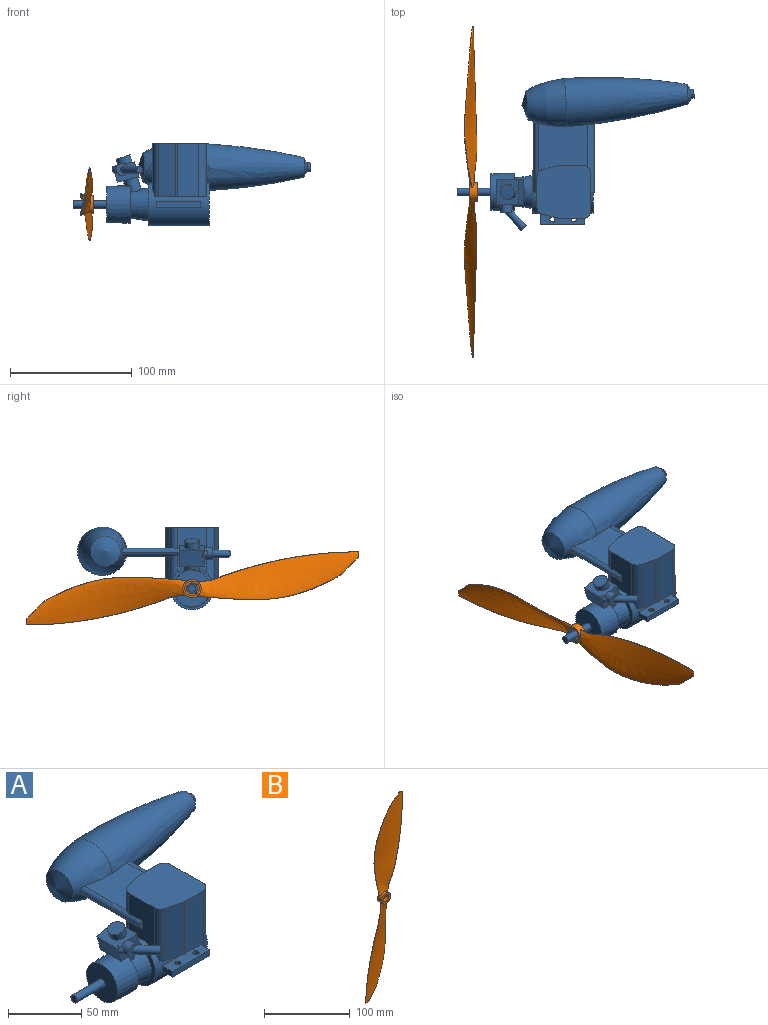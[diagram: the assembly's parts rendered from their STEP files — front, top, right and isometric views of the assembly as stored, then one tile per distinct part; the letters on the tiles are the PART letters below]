
ASSEMBLY  parts=2 mates=1
PART A: 76 faces, bbox 194.5x125.9x68.3 mm
  f0: cylinder r=17.5mm len=50mm, axis (-1,0,0), area 3318.5mm2, adj f38,f39,f40,f41,f42,f43,f47,f48
  f1: cylinder r=3mm len=18.55mm, axis (-0.68,0.74,0), area 335.6mm2, adj f2,f4,f12
  f2: plane 6x4.42mm, normal (0.68,-0.74,0), area 28.3mm2, adj f1
  f3: plane 20.3x16.69mm, normal (0,-1,0), area 153.9mm2, adj f4,f5,f6,f7,f8,f16
  f4: cylinder r=4.89mm len=9.78mm, axis (0,1,0), area 186.2mm2, adj f1,f3,f9,f11,f12,f16
  f5: plane 20.56x17.83mm, normal (-0.22,0,0.98), area 252mm2, adj f3,f6,f8,f9,f10,f11,f13,f14
  f6: plane 20.56x12.88mm, normal (-0.96,0,-0.28), area 261.1mm2, adj f3,f5,f7,f9,f10,f15,f16
  f7: plane 20.62x18.15mm, normal (0.22,0,-0.98), area 258.4mm2, adj f3,f6,f8,f10,f59
  f8: plane 20.32x12.51mm, normal (0.95,0,0.3), area 266.3mm2, adj f3,f5,f7,f10
  f9: plane 3.86x2.28mm, normal (0,-1,0), area 2.2mm2, adj f4,f5,f6,f16
  f10: plane 21.5x16.55mm, normal (0,1,0), area 237.9mm2, adj f5,f6,f7,f8
  f11: plane 5.69x1.69mm, normal (0,1,0), area 3.8mm2, adj f4,f5
  f12: plane 9.78x8.96mm, normal (0,-1,0), area 46.2mm2, adj f1,f4
  f13: plane 1.05x0.96mm, normal (-0.68,0.74,0), area 0.1mm2, adj f5,f14
  f14: cylinder r=3mm len=1.46mm, axis (-0.68,0.74,0), area 0.6mm2, adj f5,f13
  f15: plane 4.77x1.82mm, normal (-0.68,0.74,0), area 5.2mm2, adj f6,f16
  f16: cylinder r=3mm len=5.95mm, axis (-0.68,0.74,0), area 26.2mm2, adj f3,f4,f6,f9,f15
  f17: plane 6.12x2.44mm, normal (0,-1,0), area 10.4mm2, adj f29,f30,f54
  f18: cone r=3.59mm half-angle=59.2deg, axis (-1,-0.07,0), area 188.1mm2, adj f19,f23
  f19: cylinder r=3.59mm len=7.33mm, axis (-1,-0.07,0), area 55.4mm2, adj f18,f20
  f20: plane 7.18x7.16mm, normal (1,0.07,0), area 40.4mm2, adj f19
  f21: cone r=0mm half-angle=70.2deg, axis (1,0.07,0), area 501.9mm2, adj f22
  f22: revolved ~39.86x39.85mm, area 3408.9mm2, adj f21,f23,f24,f25,f29,f30
  f23: revolved ~101.71x40.61mm, area 9871mm2, adj f18,f22,f24,f25,f27,f28
  f24: plane 40.69x39.9mm, normal (0,0,-1), area 1339.5mm2, adj f22,f23,f27,f29,f32,f33,f34,f40
  f25: plane 40.76x40.24mm, normal (0,0,1), area 1330.5mm2, adj f22,f23,f28,f30,f50,f51,f52,f55
  f26: plane 5.19x2.82mm, normal (0,-1,0), area 8.8mm2, adj f27,f28,f53
  f27: cylinder r=6.67mm len=56.25mm, axis (0,-1,0), area 327.2mm2, adj f23,f24,f26,f28,f41,f53
  f28: cylinder r=6.67mm len=56.25mm, axis (0,-1,0), area 326.4mm2, adj f23,f25,f26,f27,f53,f56
  f29: cylinder r=3.68mm len=57.78mm, axis (0,-1,0), area 290.2mm2, adj f17,f22,f24,f30,f40,f54
  f30: cylinder r=3.68mm len=57.78mm, axis (0,-1,0), area 288.7mm2, adj f17,f22,f25,f29,f54,f55
  f31: plane 44x44mm, normal (0,0,1), area 1815.3mm2, adj f35,f36,f37,f42,f43,f50,f51,f52
  f32: plane 20.21x13.53mm, normal (-0.25,0.97,0), area 282.5mm2, adj f24,f33,f39,f40
  f33: cylinder r=6.35mm len=20.21mm, axis (0,0,-1), area 32.5mm2, adj f24,f32,f34,f39
  f34: plane 20.21x17.77mm, normal (0,1,0), area 359.1mm2, adj f24,f33,f39,f41
  f35: plane 43.65x17.77mm, normal (0,-1,0), area 775.5mm2, adj f31,f36,f38,f42
  f36: cylinder r=6.35mm len=43.65mm, axis (0,0,-1), area 70.1mm2, adj f31,f35,f37,f38
  f37: plane 43.65x13.53mm, normal (-0.25,-0.97,0), area 610.1mm2, adj f31,f36,f38,f43
  f38: plane 42.42x5.69mm, normal (0,0,-1), area 192.2mm2, adj f0,f35,f36,f37,f42,f43
  f39: plane 42.42x5.69mm, normal (0,0,-1), area 192.2mm2, adj f0,f32,f33,f34,f40,f41
  f40: cylinder r=6.35mm len=20.42mm, axis (0,0,-1), area 153.9mm2, adj f0,f24,f29,f32,f39,f54
  f41: cylinder r=6.35mm len=20.89mm, axis (0,0,-1), area 203.3mm2, adj f0,f24,f27,f34,f39,f53
  f42: cylinder r=6.35mm len=43.65mm, axis (0,0,-1), area 434.9mm2, adj f0,f31,f35,f38,f53
  f43: cylinder r=6.35mm len=43.65mm, axis (0,0,-1), area 349.6mm2, adj f0,f31,f37,f38,f54
  f44: plane 6x6mm, normal (-1,0,0), area 28.3mm2, adj f45
  f45: cylinder r=3mm len=27mm, axis (1,0,0), area 508.9mm2, adj f44,f49
  f46: plane 31.12x30.02mm, normal (1,0,0), area 294.5mm2, adj f57,f58,f59
  f47: plane 35x35mm, normal (-1,0,0), area 389.6mm2, adj f0,f57
  f48: plane 35x35mm, normal (1,0,0), area 962.1mm2, adj f0
  f49: plane 30x30mm, normal (-1,0,0), area 678.6mm2, adj f45,f58
  f50: plane 16.9x13.53mm, normal (-0.25,0.97,0), area 236.2mm2, adj f25,f31,f51,f55
  f51: cylinder r=6.35mm len=16.9mm, axis (0,0,-1), area 27.1mm2, adj f25,f31,f50,f52
  f52: plane 17.77x16.9mm, normal (0,1,0), area 300.3mm2, adj f25,f31,f51,f56
  f53: plane 42.17x31.3mm, normal (1,0,0), area 1019.1mm2, adj f0,f26,f27,f28,f31,f41,f42,f56
  f54: plane 37.41x24.31mm, normal (-1,0,0), area 749.1mm2, adj f0,f17,f29,f30,f31,f40,f43,f55
  f55: cylinder r=6.35mm len=17.11mm, axis (0,0,-1), area 141.9mm2, adj f25,f30,f31,f50,f54
  f56: cylinder r=6.35mm len=17.57mm, axis (0,0,-1), area 170.7mm2, adj f25,f28,f31,f52,f53
  f57: cone r=13.5mm half-angle=7.9deg, axis (1,0,0), area 1052.2mm2, adj f46,f47,f59
  f58: cone r=15.51mm half-angle=1.5deg, axis (1,0,0), area 1834.1mm2, adj f46,f49,f59
  f59: cylinder r=6mm len=15.01mm, axis (0.31,0,-0.95), area 321.3mm2, adj f7,f46,f57,f58
  f60: cylinder r=6mm len=13.39mm, axis (0.31,0,-0.95), area 219.8mm2, adj f5,f61
  f61: plane 12x11.41mm, normal (-0.31,0,0.95), area 113.1mm2, adj f60
  f62: plane 36.23x4.69mm, normal (0,1,0), area 169.9mm2, adj f63,f64,f65,f66
  f63: plane 36.23x9.58mm, normal (0,0,-1), area 317.8mm2, adj f0,f62,f64,f66,f74,f75
  f64: plane 9.58x4.69mm, normal (-1,0,0), area 44.5mm2, adj f0,f62,f63,f65
  f65: plane 36.23x9.58mm, normal (0,0,1), area 317.8mm2, adj f0,f62,f64,f66,f74,f75
  f66: plane 9.58x4.69mm, normal (1,0,0), area 44.5mm2, adj f0,f62,f63,f65
  f67: plane 36.23x9.58mm, normal (0,0,1), area 317.8mm2, adj f0,f69,f70,f71,f72,f73
  f68: plane 36.23x9.58mm, normal (0,0,-1), area 317.8mm2, adj f0,f69,f70,f71,f72,f73
  f69: plane 9.58x4.69mm, normal (1,0,0), area 44.5mm2, adj f0,f67,f68,f71
  f70: plane 9.58x4.69mm, normal (-1,0,0), area 44.5mm2, adj f0,f67,f68,f71
  f71: plane 36.23x4.69mm, normal (0,-1,0), area 169.9mm2, adj f67,f68,f69,f70
  f72: cylinder r=2.16mm len=4.69mm, axis (0,0,1), area 63.6mm2, adj f67,f68
  f73: cylinder r=2.16mm len=4.69mm, axis (0,0,1), area 63.6mm2, adj f67,f68
  f74: cylinder r=2.16mm len=4.69mm, axis (0,0,1), area 63.6mm2, adj f63,f65
  f75: cylinder r=2.16mm len=4.69mm, axis (0,0,1), area 63.6mm2, adj f63,f65
PART B: 10 faces, bbox 60.3x11.1x272.7 mm
  f0: bspline ~132.54x39.23mm, area 6340mm2, adj f1,f3
  f1: plane 5.21x1.04mm, normal (0,0,1), area 2mm2, adj f0
  f2: plane 15x15mm, normal (0,1,0), area 63.6mm2, adj f3,f7
  f3: cylinder r=7.5mm len=15mm, axis (0,-1,0), area 230.5mm2, adj f0,f2,f4,f9
  f4: plane 15x15mm, normal (0,-1,0), area 113.1mm2, adj f3,f5
  f5: cylinder r=4.5mm len=9mm, axis (0,-1,0), area 155.5mm2, adj f4,f6
  f6: plane 12x12mm, normal (0,1,0), area 49.5mm2, adj f5,f7
  f7: cylinder r=6mm len=12mm, axis (0,-1,0), area 37.7mm2, adj f2,f6
  f8: plane 5.21x1.04mm, normal (0,0,-1), area 2mm2, adj f9
  f9: bspline ~132.54x39.23mm, area 6349.3mm2, adj f3,f8
PLACE A at identity
PLACE B rot(axis=(-0.58,0.58,0.58),120deg) t=(-44.22,-3.8,-5)mm
MATE cylindrical B.f3 <-> A.f0  axis (1,0,0) through (-46.47,0,0)mm
